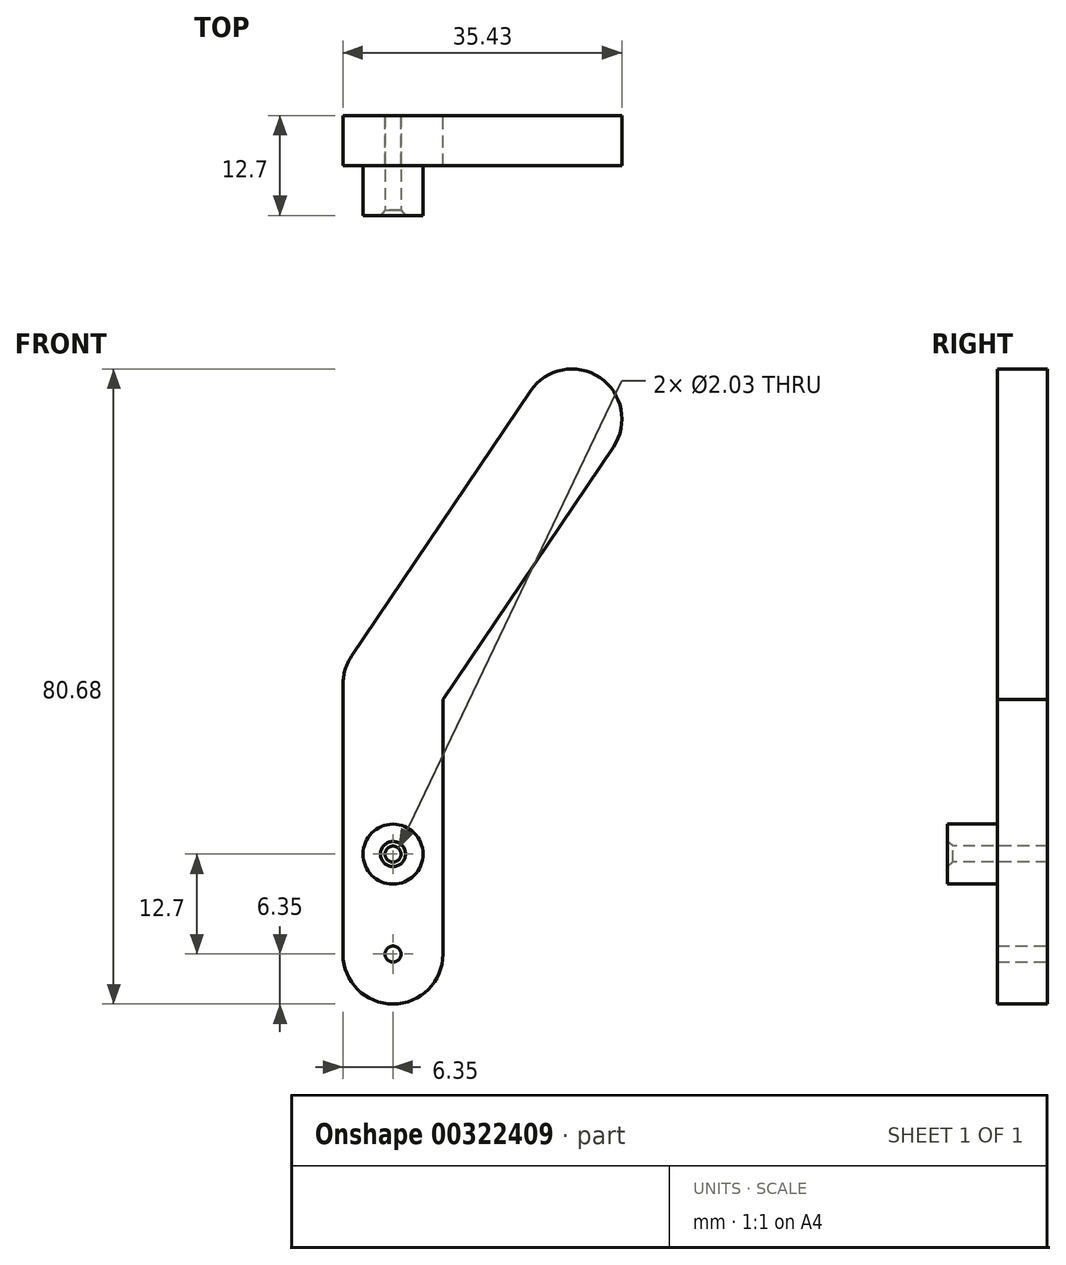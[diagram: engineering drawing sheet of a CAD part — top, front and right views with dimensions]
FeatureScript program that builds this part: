
annotation { "Feature Type Name" : "Feature", "Feature Type Description" : "" }
export const myFeature = defineFeature(function(context is Context, id is Id, definition is map)
    precondition{}
    {
        {
            var Q0;
            Q0=qCreatedBy(makeId("Front.planeOp"),FACE);
            var sketch = newSketch(context, id + "F0", { "sketchPlane" : qUnion([Q0])});
            skLineSegment(sketch, "E0", {"start": v(0, 0) * mm, "end": v(22.73, 33.7) * mm});
            skLineSegment(sketch, "E1", {"start": v(0, 0) * mm, "end": v(0, -21.59) * mm});
            skLineSegment(sketch, "E2", {"start": v(0, -21.59) * mm, "end": v(0, -34.3) * mm});
            skArc(sketch, "E3.0.startCap", {"start": v(5.26, -3.55) * mm, "mid": v(-3.55, -5.26) * mm, "end": v(-5.26, 3.55) * mm});
            skArc(sketch, "E3.0.endCap", {"start": v(17.46, 37.24) * mm, "mid": v(26.28, 38.96) * mm, "end": v(27.99, 30.14) * mm});
            skLineSegment(sketch, "E3.0.left", {"start": v(-5.26, 3.55) * mm, "end": v(17.46, 37.24) * mm});
            skLineSegment(sketch, "E3.0.right", {"start": v(5.26, -3.55) * mm, "end": v(27.99, 30.14) * mm});
            skArc(sketch, "E3.1.startCap", {"start": v(-6.35, -21.59) * mm, "mid": v(0, -15.24) * mm, "end": v(6.35, -21.59) * mm});
            skArc(sketch, "E3.1.endCap", {"start": v(6.35, -34.3) * mm, "mid": v(0, -40.64) * mm, "end": v(-6.35, -34.3) * mm});
            skLineSegment(sketch, "E3.1.left", {"start": v(6.35, -21.59) * mm, "end": v(6.35, -34.3) * mm});
            skLineSegment(sketch, "E3.1.right", {"start": v(-6.35, -21.59) * mm, "end": v(-6.35, -34.3) * mm});
            skArc(sketch, "E3.2.startCap", {"start": v(-6.35, 0) * mm, "mid": v(0, 6.35) * mm, "end": v(6.35, 0) * mm});
            skArc(sketch, "E3.2.endCap", {"start": v(6.35, -21.59) * mm, "mid": v(0, -27.94) * mm, "end": v(-6.35, -21.59) * mm});
            skLineSegment(sketch, "E3.2.left", {"start": v(6.35, 0) * mm, "end": v(6.35, -21.59) * mm});
            skLineSegment(sketch, "E3.2.right", {"start": v(-6.35, 0) * mm, "end": v(-6.35, -21.59) * mm});
            skSolve(sketch);
        }
        {
            var Q0;
            Q0 = qSketchRegion(id + "F0", true);
            extrude(context, id + "F1", {"entities" : qUnion([Q0]), "depth" : 6.35 * mm});
        }
        {
            var Q0;
            Q0=makeQuery(id+"F1.opExtrude","CAP_FACE",FACE,{"disambiguationData":[OSD([sQuery(id+"F0.wireOp",EDGE,"E3.0.endCap"),sQuery(id+"F0.wireOp",EDGE,"E3.0.left"),sQuery(id+"F0.wireOp",EDGE,"E3.0.right"),sQuery(id+"F0.wireOp",EDGE,"E3.1.endCap"),sQuery(id+"F0.wireOp",EDGE,"E3.1.left"),sQuery(id+"F0.wireOp",EDGE,"E3.1.right"),sQuery(id+"F0.wireOp",EDGE,"E3.2.startCap"),sQuery(id+"F0.wireOp",EDGE,"E3.2.left"),sQuery(id+"F0.wireOp",EDGE,"E3.2.right")])],"isStart":false});
            var sketch = newSketch(context, id + "F2", { "sketchPlane" : qUnion([Q0])});
            skCircle(sketch, "E4", {"center": v(0, -21.59) * mm, "radius": 3.8 * mm});
            skSolve(sketch);
        }
        {
            var Q0;
            Q0 = qSketchRegion(id + "F2", true);
            extrude(context, id + "F3", {"entities" : qUnion([Q0]), "operationType" : NewBodyOperationType.ADD, "depth" : 6.35 * mm});
        }
        {
            var Q0;
            Q0=makeQuery(id+"F3.opExtrude","CAP_FACE",FACE,{"disambiguationData":[OSD([sQuery(id+"F2.wireOp",EDGE,"E4")])],"isStart":false});
            var sketch = newSketch(context, id + "F4", { "sketchPlane" : qUnion([Q0])});
            skLineSegment(sketch, "E5", {"start": v(0, -21.59) * mm, "end": v(0, -34.3) * mm});
            skCircle(sketch, "E6", {"center": v(0, -34.3) * mm, "radius": 1.02 * mm});
            skPoint(sketch, "E7", {"position": v(0, -21.59) * mm});
            skSolve(sketch);
        }
        {
            var Q0;
            Q0=sQuery(id+"F4.wireOp",VERTEX,"E7");
            var Q1;
            Q1=makeQuery(id+"F1.opExtrude","SWEPT_BODY",BODY,{"disambiguationData":[OSD([sQuery(id+"F0.wireOp",EDGE,"E3.0.endCap"),sQuery(id+"F0.wireOp",EDGE,"E3.0.left"),sQuery(id+"F0.wireOp",EDGE,"E3.0.right"),sQuery(id+"F0.wireOp",EDGE,"E3.1.endCap"),sQuery(id+"F0.wireOp",EDGE,"E3.1.left"),sQuery(id+"F0.wireOp",EDGE,"E3.1.right"),sQuery(id+"F0.wireOp",EDGE,"E3.2.startCap"),sQuery(id+"F0.wireOp",EDGE,"E3.2.left"),sQuery(id+"F0.wireOp",EDGE,"E3.2.right")])]});
            hole(context, id + "F5", {"style" : HoleStyle.C_SINK, "endStyle" : HoleEndStyle.THROUGH, "holeDiameter" : 2.03 * mm, "cSinkDiameter" : 3.17 * mm, "cSinkAngle" : 82 * degree, "tappedDepth" : 12.7 * mm, "tapClearance" : 3, "locations" : qUnion([Q0]), "scope" : qUnion([Q1])});
        }
        {
            var Q0;
            Q0=sQuery(id+"F0.wireOp",VERTEX,"E2.end");
            var Q1;
            Q1=makeQuery(id+"F1.opExtrude","SWEPT_BODY",BODY,{"disambiguationData":[OSD([sQuery(id+"F0.wireOp",EDGE,"E3.0.endCap"),sQuery(id+"F0.wireOp",EDGE,"E3.0.left"),sQuery(id+"F0.wireOp",EDGE,"E3.0.right"),sQuery(id+"F0.wireOp",EDGE,"E3.1.endCap"),sQuery(id+"F0.wireOp",EDGE,"E3.1.left"),sQuery(id+"F0.wireOp",EDGE,"E3.1.right"),sQuery(id+"F0.wireOp",EDGE,"E3.2.startCap"),sQuery(id+"F0.wireOp",EDGE,"E3.2.left"),sQuery(id+"F0.wireOp",EDGE,"E3.2.right")])]});
            hole(context, id + "F6", {"style" : HoleStyle.SIMPLE, "endStyle" : HoleEndStyle.THROUGH, "oppositeDirection" : true, "holeDiameter" : 2.03 * mm, "tappedDepth" : 12.7 * mm, "tapClearance" : 3, "locations" : qUnion([Q0]), "scope" : qUnion([Q1])});
        }
    });
